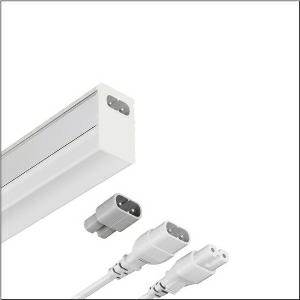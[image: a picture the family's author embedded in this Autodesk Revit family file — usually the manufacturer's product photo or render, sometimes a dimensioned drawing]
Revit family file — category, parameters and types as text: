
# Revit family: siluette_41-e_51lp327km20ae
name_source: partatom
category: Lighting Fixtures
units: mm (PartAtom-declared; Revit-internal decimal feet)

## family parameters
Cut with Voids When Loaded = No
Host = Face
Light Source = No
Part Type = Normal
Room Calculation Point = No
Round Connector Dimension = Use Diameter
Shared = No

## types (1)
- --- (1 x LED, 2000 lm, 16 W, 5000K)
    Apparent Load = 16 VA
    CIE Flux Codes = 37 66 87 87 100
    Color Rendering = 80
    Color Temperature = 5000K
    Default Elevation = 1800 mm
    Description = Siluette 41-E, batten luminaire, primary optical cover: cover, of PC, frosted, light emission: direct distribution, primary light characteristic: symmetric, installation type: surface-mounted, LED, rated luminous flux: 2.000lm, luminous efficacy: 125lm/W, light colour: 830/840/850, colour temperature: 3000/4000/5000K, control gear: ON/OFF, with system connector: socket, mains connection: 220..240V, AC, 50/60Hz, rated input power: 16W, housing, of aluminium, silver, length: 1.180mm, width: 25mm, height: 44mm, end cap, of PC, white, protection rating (complete): IP20, insulation class (complete): insulation class II (safety insulation), certification: CE, permissible operating ambient temperature: -20..+40°C, packaging unit: 1 piece
    Height = 44 mm
    Lamp = 1 x LED
    Lamp Light Flux = 2000 lm
    Lamp Power = 16 W
    Lamp count = 1
    Length = 1180 mm
    Luminous efficacy = 125 lm/W
    Manufacturer = Siteco
    ModVariant = No
    Model = 51LP327KM20AE
    Mounting Place = Ceiling
    Mounting Type = Surface mounted
    Number of Poles = 1
    OnlyDefault = Yes
    Power Factor = 1
    Product Name = Siluette 41-E
    Product group = batten luminaire
    ProductGroupID = 303
    Protection Class = Protection class II
    Protection Degree = IP 20
    RLX_Detail_Level = 1
    RLX_Emergency_Light_Flux = 0 lm
    RLX_Emergency_Type = 0
    RLX_Emergency_Type_DB = No
    RlxData = <blob elided: 37405 chars, md5=01ec29d5>
    Socket = socket
    Standby Power = 0 W
    System Light Flux = 2000 lm
    System Power = 16 W
    Type Comments = individual setting: colour temperature 5000K
    Type Image = l_1007257.jpg
    URL = http://relux.com
    VarID = @adj_037597
    Voltage = 0 V
    Weight = 0.00 kg
    Width = 25 mm  [stored 0.082021 ft]

note: [stored X ft] marks values corroborated as IEEE doubles in the binary element streams (Revit-internal decimal feet)

## geometry (parser evidence)
native form markers: Blend x4, Sweep x13
no freeform markers — native parametric forms only
